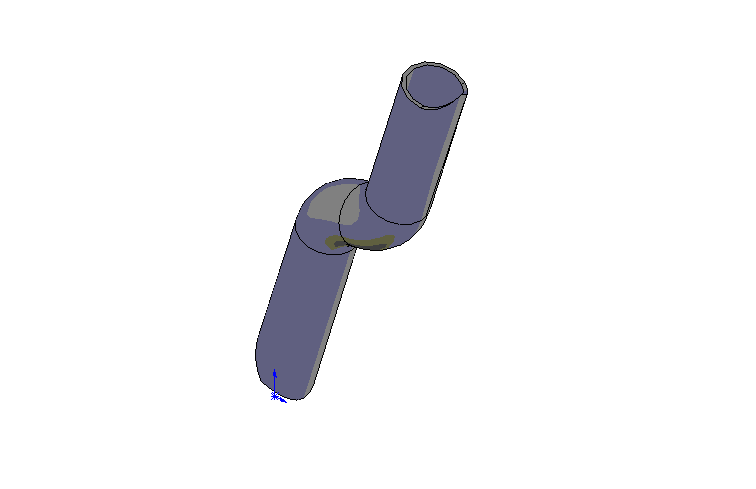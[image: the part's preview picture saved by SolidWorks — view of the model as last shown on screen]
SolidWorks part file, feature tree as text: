
SOLIDWORKS PART (.sldprt)
format: sldprt  version: not decoded by parser v0  size: 378,880 bytes
history: native  units: mm
features: plane x11, sketch x10, cut_extrude x2, material x1, sweep x1 (+10 scaffold rows collapsed)
feature tree (35):
  scaffold x10  (default folders/planes/origin — collapsed)
  material  "Matériau <non spécifié>"
  plane  "Plan de face"
  plane  "Plan de dessus"
  plane  "Plan de droite"
  sketch  "Esquisse1"  dims[c1.D1=625.0mm c1.D2=460.0mm c1.D3=545.0mm c1.D4=27.0mm c1.D5=500.0mm c1.D6=445.0mm c1.D7=670.0mm c2.D1=622.0mm c2.D2=670.0mm c2.D3=545.0mm c2.D4=460.0mm c2.D5=445.0mm c2.D6=495.0mm c2.D7=535.0mm c2.D8=27.0mm c2.D9=8.0mm c2.D10=155.0mm c2.D11=400.0mm c2.D12=~545.374305mm c3.D12=56.0deg]
  plane  "Plan1"
  plane  "Plan2"  Offset=180mm
  plane  "Plan3"  Offset=340mm
  plane  "Plan4"  Offset=500mm
  plane  "Plan5"
  plane  "Plan6"
  plane  "Plan7"  Offset=500mm
  plane  "Plan8"  Offset=287mm
  sketch  "Esquisse2"  dims[D2=30.0mm D1=33.0mm D3=120.0mm]
  sketch  "Esquisse3"  dims[D1=32.0mm D2=28.0mm]
  sweep  "Balayage4"
  sketch  "Esquisse4"  dims[D1=42.5mm]
  cut_extrude  "Enlèv. mat.-Extru.7"  [1 undecoded]
  sketch  "Esquisse12"  dims[D3=10.0mm D4=25.0mm D1=65.0mm D2=65.0mm D6=255.0mm D7=16.0mm D5=3.0mm]
  cut_extrude  "Enlèv. mat.-Extru.8"  [1 undecoded]
  sketch  "Esquisse5"  dims[c1.D1=42.0mm c1.D2=55.0mm c1.D3=2.0mm c1.D4=~8.95384mm c2.D3=2.0mm c2.D4=2.0mm]
  sketch  "Esquisse6"  dims[D1=50.0mm D2=46.0mm]
  sketch  "Esquisse7"  dims[D1=46.0mm]
  sketch  "Esquisse8"
  sketch  "Esquisse9"  dims[D1=45.0mm]
decode coverage: 9 of 13 modeling features carry decoded parameters
note: ~ marks probable driven/reference dimensions
note: 2 parameter values undecoded
note: suppression state not decoded; provenance and decode notes live in map.json
